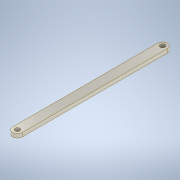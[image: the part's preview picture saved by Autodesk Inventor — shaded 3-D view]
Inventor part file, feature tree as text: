
AUTODESK INVENTOR PART (.ipt)
format: ipt  version: 2022 (Build 260153000, 153)  size: 120,320 bytes
history: native  units: in
note: dims shown in document units (in); Inventor stores cm internally (conversion verified against a paired STEP export)
features: extrude x3, sketch x2
ambient origin geometry x8: Origin, YZ Plane, XZ Plane, XY Plane, X Axis, Y Axis, Z Axis, Center Point
bodies: Solido1 (feature_tree)
feature tree (5):
  extrude  "Estrusione1"  Depth=5.9055in
  sketch  "Schizzo2"
  extrude  "Estrusione2"  Depth=0.3937in
  extrude  "Estrusione3"  Depth=0.1575in TaperAngle=0.0deg
  sketch  "Schizzo1"
